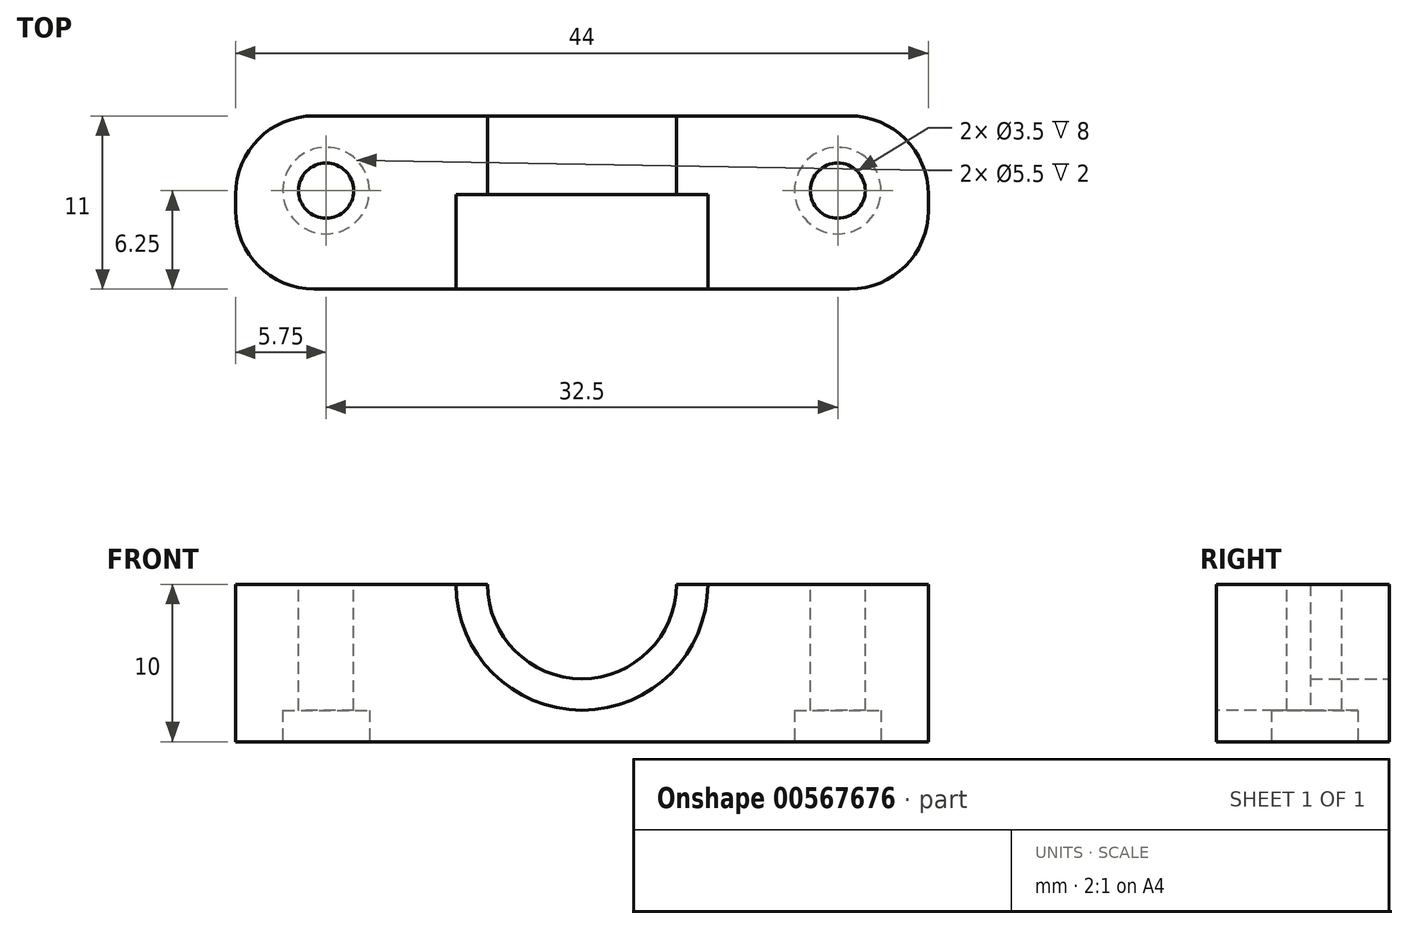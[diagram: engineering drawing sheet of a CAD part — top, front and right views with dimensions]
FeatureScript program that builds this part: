
annotation { "Feature Type Name" : "Feature", "Feature Type Description" : "" }
export const myFeature = defineFeature(function(context is Context, id is Id, definition is map)
    precondition{}
    {
        {
            var Q0;
            Q0=qCreatedBy(makeId("Top.planeOp"),FACE);
            var sketch = newSketch(context, id + "F0", { "sketchPlane" : qUnion([Q0])});
            skLineSegment(sketch, "E0.bottom", {"start": v(0, 0) * mm, "end": v(40, 0) * mm});
            skLineSegment(sketch, "E0.top", {"start": v(0, 11) * mm, "end": v(40, 11) * mm});
            skLineSegment(sketch, "E0.left", {"start": v(0, 0) * mm, "end": v(0, 11) * mm});
            skLineSegment(sketch, "E0.right", {"start": v(40, 0) * mm, "end": v(40, 11) * mm});
            skSolve(sketch);
        }
        {
            var Q0;
            Q0=qSketchRegion(id+"F0",true);
            extrude(context, id + "F1", {"entities" : qUnion([Q0]), "depth" : 10 * mm});
        }
        {
            var Q0;
            Q0=makeQuery(id+"F1.opExtrude","SWEPT_FACE",FACE,{"disambiguationData":[OSD([sQuery(id+"F0.wireOp",EDGE,"E0.bottom")])]});
            var sketch = newSketch(context, id + "F2", { "sketchPlane" : qUnion([Q0])});
            skCircle(sketch, "E1", {"center": v(20, 10) * mm, "radius": 8 * mm});
            skSolve(sketch);
        }
        {
            var Q0;
            Q0=qSketchRegion(id+"F2",true);
            extrude(context, id + "F3", {"entities" : qUnion([Q0]), "operationType" : NewBodyOperationType.REMOVE, "oppositeDirection" : true, "depth" : 6 * mm});
        }
        {
            var Q0;
            Q0=makeQuery(id+"F1.opExtrude","SWEPT_FACE",FACE,{"disambiguationData":[OSD([sQuery(id+"F0.wireOp",EDGE,"E0.top")])]});
            var sketch = newSketch(context, id + "F4", { "sketchPlane" : qUnion([Q0])});
            skCircle(sketch, "E2", {"center": v(-20, 10) * mm, "radius": 6 * mm});
            skSolve(sketch);
        }
        {
            var Q0;
            Q0=qSketchRegion(id+"F4",true);
            extrude(context, id + "F5", {"entities" : qUnion([Q0]), "operationType" : NewBodyOperationType.REMOVE, "oppositeDirection" : true, "depth" : 6 * mm});
        }
        {
            var Q0;
            Q0=makeQuery(id+"F1.opExtrude","SWEPT_FACE",FACE,{"disambiguationData":[OSD([sQuery(id+"F0.wireOp",EDGE,"E0.left")])]});
            var sketch = newSketch(context, id + "F6", { "sketchPlane" : qUnion([Q0])});
            skLineSegment(sketch, "E3.bottom", {"start": v(-11, 0) * mm, "end": v(0, 0) * mm});
            skLineSegment(sketch, "E3.top", {"start": v(-11, 10) * mm, "end": v(0, 10) * mm});
            skLineSegment(sketch, "E3.left", {"start": v(-11, 0) * mm, "end": v(-11, 10) * mm});
            skLineSegment(sketch, "E3.right", {"start": v(0, 0) * mm, "end": v(0, 10) * mm});
            skSolve(sketch);
        }
        {
            var Q0;
            Q0=qSketchRegion(id+"F6",true);
            extrude(context, id + "F7", {"entities" : qUnion([Q0]), "operationType" : NewBodyOperationType.ADD, "depth" : 2 * mm});
        }
        {
            var Q0;
            Q0=makeQuery(id+"F1.opExtrude","SWEPT_FACE",FACE,{"disambiguationData":[OSD([sQuery(id+"F0.wireOp",EDGE,"E0.right")])]});
            var sketch = newSketch(context, id + "F8", { "sketchPlane" : qUnion([Q0])});
            skLineSegment(sketch, "E4.bottom", {"start": v(11, 10) * mm, "end": v(0, 10) * mm});
            skLineSegment(sketch, "E4.top", {"start": v(11, 0) * mm, "end": v(0, 0) * mm});
            skLineSegment(sketch, "E4.left", {"start": v(11, 10) * mm, "end": v(11, 0) * mm});
            skLineSegment(sketch, "E4.right", {"start": v(0, 10) * mm, "end": v(0, 0) * mm});
            skSolve(sketch);
        }
        {
            var Q0;
            Q0=qSketchRegion(id+"F8",true);
            extrude(context, id + "F9", {"entities" : qUnion([Q0]), "operationType" : NewBodyOperationType.ADD, "depth" : 2 * mm});
        }
        {
            var Q0;
            Q0=makeQuery(id+"F9.opExtrude","CAP_EDGE",EDGE,{"disambiguationData":[OSD([sQuery(id+"F8.wireOp",EDGE,"E4.left")])],"isStart":false});
            var Q1;
            Q1=makeQuery(id+"F9.opExtrude","CAP_EDGE",EDGE,{"disambiguationData":[OSD([sQuery(id+"F8.wireOp",EDGE,"E4.right")])],"isStart":false});
            var Q2;
            Q2=makeQuery(id+"F7.opExtrude","CAP_EDGE",EDGE,{"disambiguationData":[OSD([sQuery(id+"F6.wireOp",EDGE,"E3.left")])],"isStart":false});
            var Q3;
            Q3=makeQuery(id+"F7.opExtrude","CAP_EDGE",EDGE,{"disambiguationData":[OSD([sQuery(id+"F6.wireOp",EDGE,"E3.right")])],"isStart":false});
            fillet(context, id + "F10", {"entities" : qUnion([Q0, Q1, Q2, Q3]), "radius" : 5 * mm, "tangentPropagation" : true, "allowEdgeOverflow" : false});
        }
        {
            var Q0;
            {var subQ0=sQuery(id+"F0.wireOp",EDGE,"E0.bottom");var subQ1=sQuery(id+"F0.wireOp",EDGE,"E0.top");var subQ2=sQuery(id+"F0.wireOp",EDGE,"E0.left");Q0=makeQuery(id+"F5.boolean.opBoolean","SPLIT",FACE,{"disambiguationData":[TD([makeQuery(id+"F1.opExtrude","SWEPT_FACE",FACE,{"disambiguationData":[OSD([subQ2])]})])],"derivedFrom":makeQuery(id+"F1.opExtrude","CAP_FACE",FACE,{"disambiguationData":[OSD([subQ0,subQ1,subQ2,sQuery(id+"F0.wireOp",EDGE,"E0.right")])],"isStart":false})});}
            var sketch = newSketch(context, id + "F11", { "sketchPlane" : qUnion([Q0])});
            skCircle(sketch, "E5", {"center": v(3.75, 6.25) * mm, "radius": 1.75 * mm});
            skCircle(sketch, "E6", {"center": v(36.25, 6.25) * mm, "radius": 1.75 * mm});
            skSolve(sketch);
        }
        {
            var Q0;
            Q0=qSketchRegion(id+"F11",true);
            extrude(context, id + "F12", {"entities" : qUnion([Q0]), "operationType" : NewBodyOperationType.REMOVE, "oppositeDirection" : true, "depth" : 25 * mm});
        }
        {
            var Q0;
            Q0=makeQuery(id+"F9.boolean.opBoolean","MERGE",FACE,{"derivedFrom":[makeQuery(id+"F7.boolean.opBoolean","MERGE",FACE,{"derivedFrom":[makeQuery(id+"F1.opExtrude","CAP_FACE",FACE,{"disambiguationData":[OSD([sQuery(id+"F0.wireOp",EDGE,"E0.bottom"),sQuery(id+"F0.wireOp",EDGE,"E0.top"),sQuery(id+"F0.wireOp",EDGE,"E0.left"),sQuery(id+"F0.wireOp",EDGE,"E0.right")])],"isStart":true}),makeQuery(id+"F7.opExtrude","SWEPT_FACE",FACE,{"disambiguationData":[OSD([sQuery(id+"F6.wireOp",EDGE,"E3.bottom")])]})]}),makeQuery(id+"F9.opExtrude","SWEPT_FACE",FACE,{"disambiguationData":[OSD([sQuery(id+"F8.wireOp",EDGE,"E4.top")])]})]});
            var sketch = newSketch(context, id + "F13", { "sketchPlane" : qUnion([Q0])});
            skCircle(sketch, "E7.0", {"center": v(3.75, -6.25) * mm, "radius": 2.75 * mm});
            skCircle(sketch, "E8.0", {"center": v(36.25, -6.25) * mm, "radius": 2.75 * mm});
            skSolve(sketch);
        }
        {
            var Q0;
            Q0=makeQuery(id+"F13.imprint","IMPRINT",FACE,{"disambiguationData":[TD([[makeQuery(id+"F13.imprint","IMPRINT",EDGE,{"derivedFrom":sQuery(id+"F13.wireOp",EDGE,"E7.0")}),1.0]])]});
            var Q1;
            Q1=makeQuery(id+"F13.imprint","IMPRINT",FACE,{"disambiguationData":[TD([[makeQuery(id+"F13.imprint","IMPRINT",EDGE,{"derivedFrom":sQuery(id+"F13.wireOp",EDGE,"E8.0")}),1.0]])]});
            extrude(context, id + "F14", {"entities" : qUnion([Q0, Q1]), "operationType" : NewBodyOperationType.REMOVE, "oppositeDirection" : true, "depth" : 2 * mm, "offsetDistance" : 25 * mm});
        }
    });
